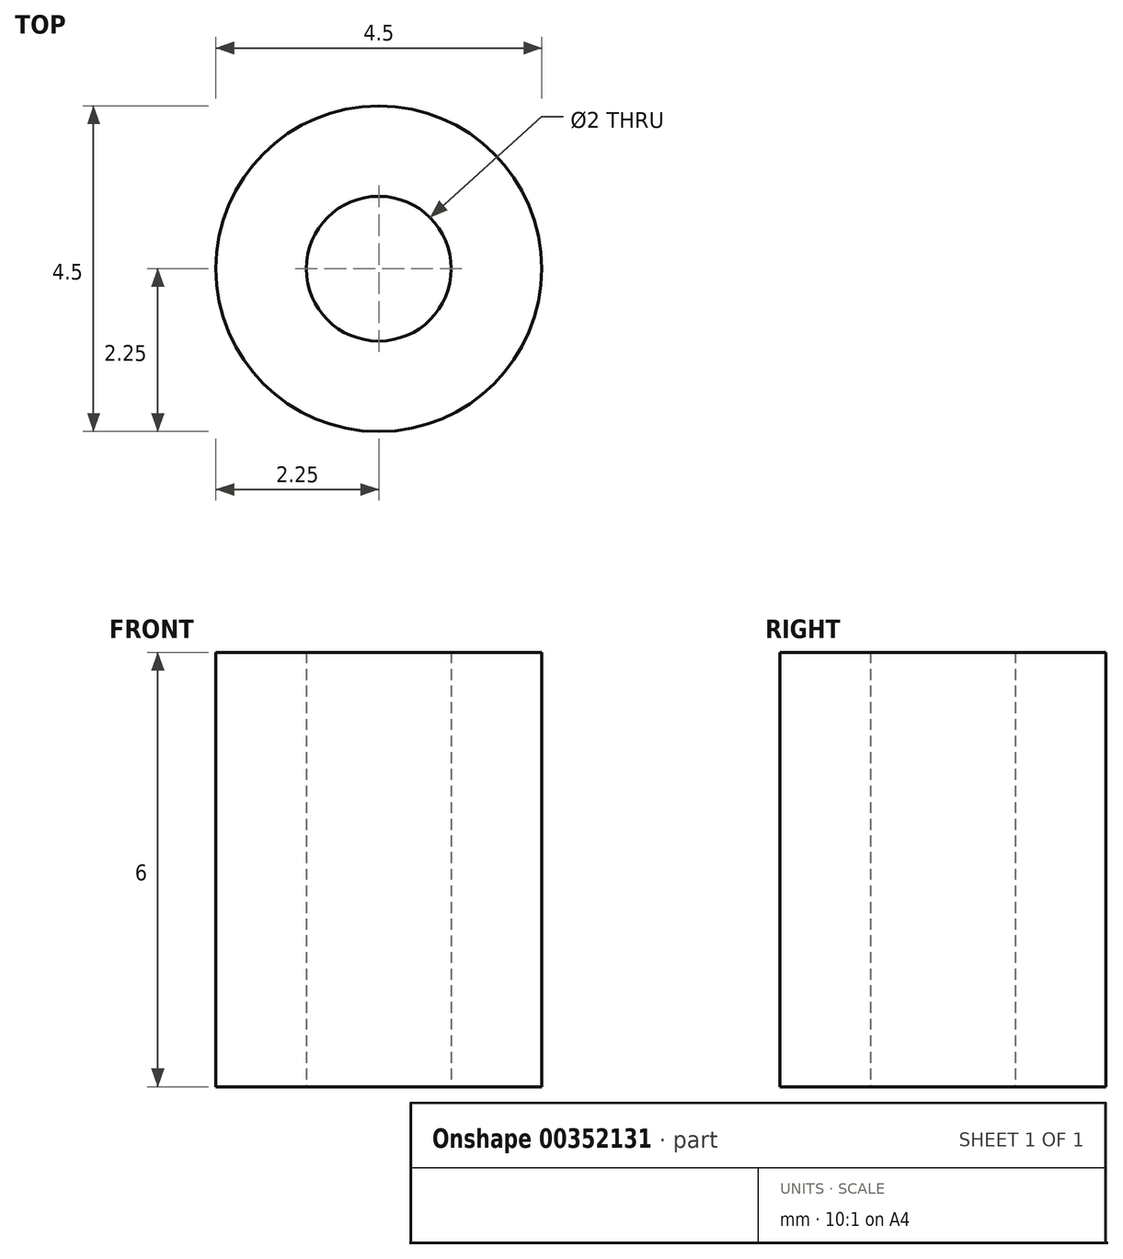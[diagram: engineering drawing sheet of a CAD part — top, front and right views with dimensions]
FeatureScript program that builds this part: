
annotation { "Feature Type Name" : "Feature", "Feature Type Description" : "" }
export const myFeature = defineFeature(function(context is Context, id is Id, definition is map)
    precondition{}
    {
        {
            var Q0;
            Q0=qCreatedBy(makeId("Top.planeOp"),FACE);
            var sketch = newSketch(context, id + "F0", { "sketchPlane" : qUnion([Q0])});
            skCircle(sketch, "E0", {"center": v(0, 0) * mm, "radius": 2.25 * mm});
            skCircle(sketch, "E1", {"center": v(0, 0) * mm, "radius": 1 * mm});
            skSolve(sketch);
        }
        {
            var Q0;
            Q0=makeQuery(id+"F0.imprint","IMPRINT",FACE,{"disambiguationData":[TD([[makeQuery(id+"F0.imprint","IMPRINT",EDGE,{"derivedFrom":sQuery(id+"F0.wireOp",EDGE,"E0")}),1.0]])]});
            extrude(context, id + "F1", {"entities" : qUnion([Q0]), "depth" : 6 * mm});
        }
    });
